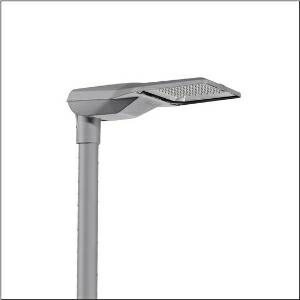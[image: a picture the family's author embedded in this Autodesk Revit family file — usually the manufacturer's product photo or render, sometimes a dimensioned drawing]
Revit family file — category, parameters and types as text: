
# Revit family: streetlight_sl_21_iq_midi___stw1_0a_5xe3e41g08nb_77a4
name_source: partatom
category: Lighting Fixtures
units: mm (PartAtom-declared; Revit-internal decimal feet)

## family parameters
Cut with Voids When Loaded = No
Host = Face
Light Source = No
Part Type = Normal
Room Calculation Point = No
Round Connector Dimension = Use Diameter
Shared = No

## types (1)
- --- (1 x LED, 24250 lm, 155.5 W, 4000K)
    Apparent Load = 155 VA
    CIE Flux Codes = 39 75 98 100 100
    Color Rendering = 70
    Color Temperature = 4000K
    Default Elevation = 1800 mm
    Description = Streetlight SL 21 iQ midi, mast luminaire, primary light control with lens, of PMMA, primary optical cover: cover, of toughened safety glass, transparent, light distribution: STW1.0a, light emission: direct distribution, primary light characteristic: asymmetric, installation type: post-top, side-entry, LED, High Power LED, rated luminous flux: 24.250lm, luminous efficacy: 156lm/W, light colour: 740, colour temperature: 4000K, control gear: iQ Street-Remote, control: Street-Remote, Auto-Match, Temp-Guard, Lumen-Switch, Night-Set, Smart-Wire, Light-Fading, Desk-Remote (wireless, voltage-free reading and setting of iQ features in the workshop via application-optimized NFC function/RFID function), optimised constant luminous flux control (CLO 2.0), pre-setting: linear dimming characteristic, mains connection: 230..240V, AC, 50/60Hz, start of lifetime: 156W, end of service life: 162W, reduction: 69W, luminaire housing, of diecast aluminium, powder-coated, SITECO metallic grey (DB 702S), corrosivity category C5 high according to DIN EN ISO 12944, please order mast flange separately, inclination adjustable: 0°, 5°, 10°, 15°, sealing non-destructively replaceable, multi-level sealing system, length: 644mm, width: 335mm, height: 110mm, mast flange for spigot size: 42mm (side-entry): 5XC10008XM4, 60/48mm (side-entry/post-top): 5XC10108XM2, 76/60mm (side-entry/post-top): 5XC10108XM1, mounting height: 4..8m, protection rating (complete): IP66, insulation class (complete): insulation class II (safety insulation), certification: CE, ENEC, ENEC+, VDE, impact resistance: IK10, permissible operating ambient temperature for outdoor applications: -40..+50°C, standard-compliant lighting for roads and squares, packaging unit: 1 piece

Light Distribution: STW1.0a
    Height = 111 mm
    Lamp = 1 x LED
    Lamp Light Flux = 24250 lm
    Lamp Power = 155.5 W
    Lamp count = 1
    Length = 644 mm
    Luminous efficacy = 156 lm/W
    Manufacturer = Siteco
    ModVariant = No
    Model = 5XE3E41G08NB
    Number of Poles = 1
    OnlyDefault = Yes
    Power Factor = 1
    Product Name = Streetlight SL 21 iQ midi | STW1.0a
    Product group = mast luminaire | pylon top
    ProductGroupID = 6100
    Protection Class = Protection class II
    Protection Degree = IP 66
    RLX_Detail_Level = 1
    RLX_Emergency_Light_Flux = 0 lm
    RLX_Emergency_Type = 0
    RLX_Emergency_Type_DB = No
    RlxData = <blob elided: 27293 chars, md5=3ba6f2fa>
    Socket = socket
    Standby Power = 0 W
    System Light Flux = 24250 lm
    System Power = 155 W
    Type Comments = factory setting: luminous flux: 100 % | dim-lin: 254 | 823 mA
    Type Image = l_1004298.jpg
    URL = http://relux.com
    VarID = @adj_169281
    Voltage = 0 V
    Weight = 0.00 kg
    Width = 336 mm

## geometry (parser evidence)
native form markers: Blend x4, Sweep x13
no freeform markers — native parametric forms only
